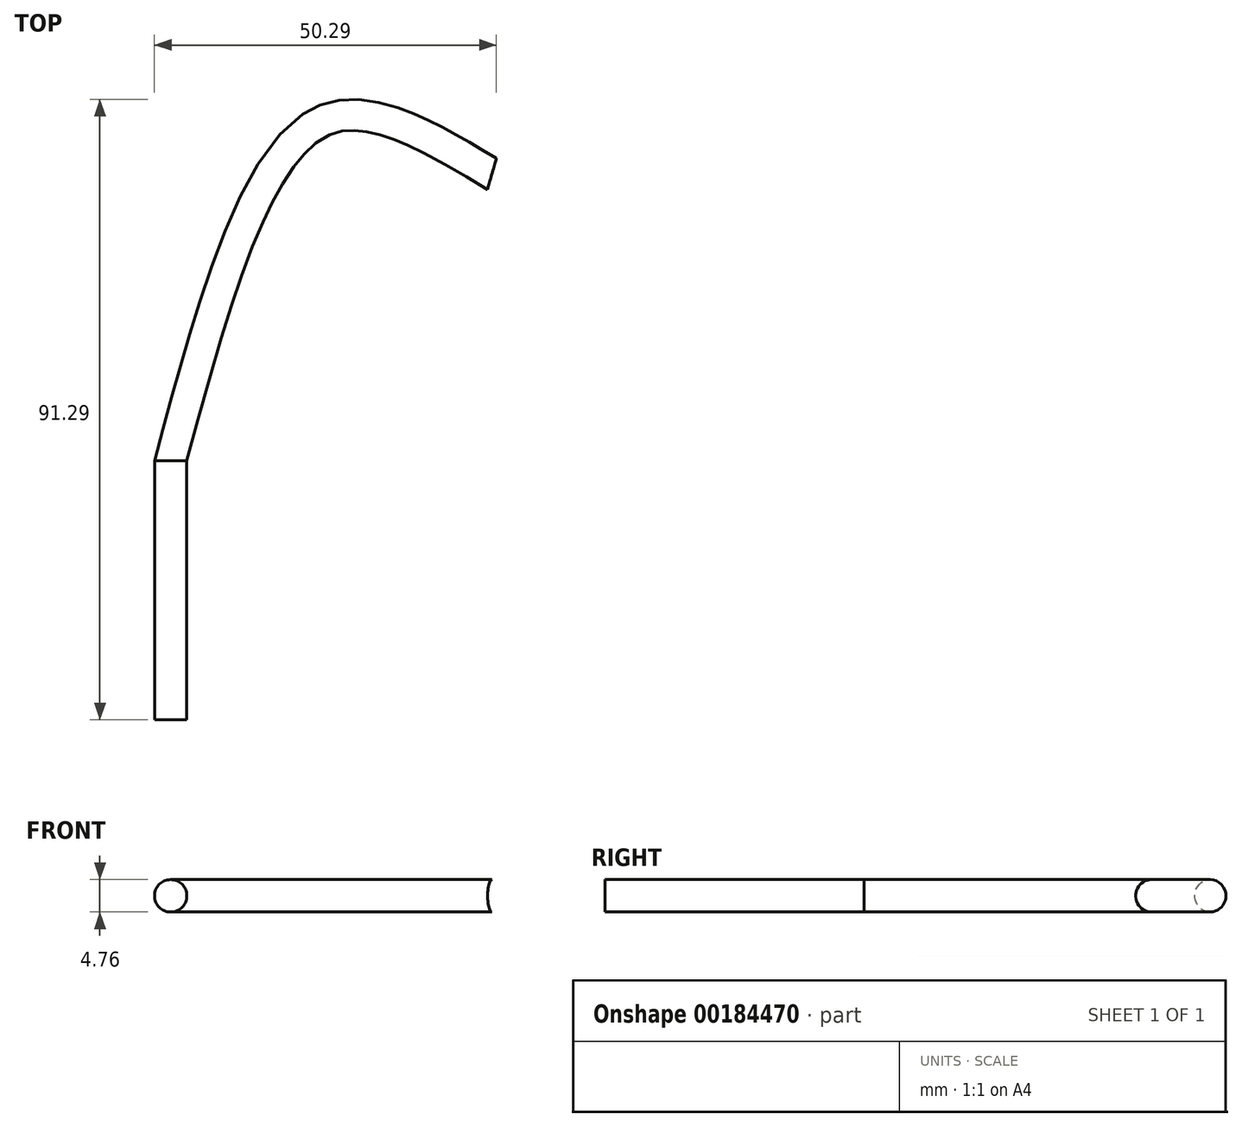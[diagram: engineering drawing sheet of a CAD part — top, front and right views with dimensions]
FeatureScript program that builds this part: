
annotation { "Feature Type Name" : "Feature", "Feature Type Description" : "" }
export const myFeature = defineFeature(function(context is Context, id is Id, definition is map)
    precondition{}
    {
        {
            var Q0;
            Q0=qCreatedBy(makeId("Front.planeOp"),FACE);
            var sketch = newSketch(context, id + "F0", { "sketchPlane" : qUnion([Q0])});
            skCircle(sketch, "E0", {"center": v(-40.17, 0) * mm, "radius": 2.38 * mm});
            skSolve(sketch);
        }
        {
            var Q0;
            Q0 = qSketchRegion(id + "F0", true);
            extrude(context, id + "F1", {"entities" : qUnion([Q0]), "depth" : 38.1 * mm});
        }
        {
            var Q0;
            Q0=qCreatedBy(makeId("Top.planeOp"),FACE);
            var sketch = newSketch(context, id + "F2", { "sketchPlane" : qUnion([Q0])});
            skFitSpline(sketch, "E1", {"points": [v(-40.8, 0) * mm, v(-18.16, 50.53) * mm, v(7.26, 42.84) * mm], "startDerivative": vector(31.3, 116.34) * mm, "endDerivative": vector(67, -40.14) * mm});
            skSolve(sketch);
        }
        {
            var Q0;
            Q0=makeQuery(id+"F1.opExtrude","CAP_FACE",FACE,{"disambiguationData":[OSD([sQuery(id+"F0.wireOp",EDGE,"E0")])],"isStart":true});
            var Q1;
            Q1=sQuery(id+"F2.wireOp",EDGE,"E1");
            var Q2;
            Q2=sQuery(id+"F2.wireOp",EDGE,"E1");
            sweep(context, id + "F3", {"operationType" : NewBodyOperationType.ADD, "profiles" : qUnion([Q0]), "surfaceProfiles" : qUnion([Q1]), "path" : qUnion([Q2])});
        }
    });
